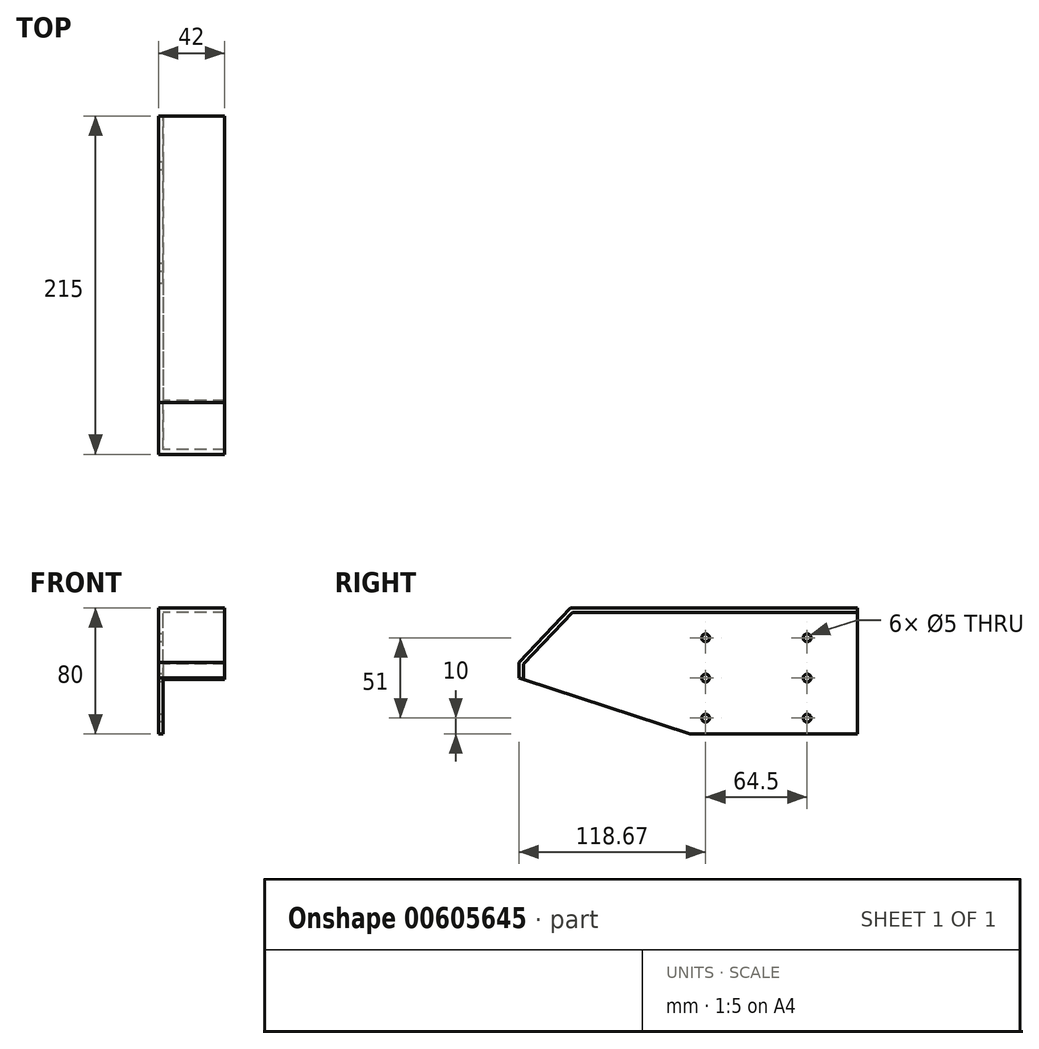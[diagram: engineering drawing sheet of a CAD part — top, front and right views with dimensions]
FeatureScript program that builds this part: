
annotation { "Feature Type Name" : "Feature", "Feature Type Description" : "" }
export const myFeature = defineFeature(function(context is Context, id is Id, definition is map)
    precondition{}
    {
        {
            var Q0;
            Q0=qCreatedBy(makeId("Right.planeOp"),FACE);
            var sketch = newSketch(context, id + "F0", { "sketchPlane" : qUnion([Q0])});
            skLineSegment(sketch, "E0.bottom", {"start": v(1.17, -40) * mm, "end": v(107.5, -40) * mm});
            skLineSegment(sketch, "E0.top", {"start": v(-74.63, 40) * mm, "end": v(107.5, 40) * mm});
            skLineSegment(sketch, "E0.right", {"start": v(107.5, -40) * mm, "end": v(107.5, 40) * mm});
            skPoint(sketch, "E0.middle", {"position": v(0, 0) * mm});
            skPoint(sketch, "E1", {"position": v(75.67, 40) * mm});
            skLineSegment(sketch, "E2", {"start": v(75.67, 40) * mm, "end": v(75.67, -40) * mm, "construction": true});
            skPoint(sketch, "E3", {"position": v(107.5, -30) * mm});
            skLineSegment(sketch, "E4", {"start": v(107.5, -30) * mm, "end": v(-107.5, -30) * mm, "construction": true});
            skCircle(sketch, "E5", {"center": v(75.67, -30) * mm, "radius": 2.5 * mm});
            skPoint(sketch, "E6", {"position": v(75.67, -4.5) * mm});
            skPoint(sketch, "E7", {"position": v(75.67, 21) * mm});
            skCircle(sketch, "E8", {"center": v(75.67, -4.5) * mm, "radius": 2.5 * mm});
            skCircle(sketch, "E9", {"center": v(75.67, 21) * mm, "radius": 2.5 * mm});
            skPoint(sketch, "E10", {"position": v(11.17, 21) * mm});
            skPoint(sketch, "E11", {"position": v(11.17, -4.5) * mm});
            skPoint(sketch, "E12", {"position": v(11.17, -30) * mm});
            skCircle(sketch, "E13", {"center": v(11.17, 21) * mm, "radius": 2.5 * mm});
            skCircle(sketch, "E14", {"center": v(11.17, -4.5) * mm, "radius": 2.5 * mm});
            skCircle(sketch, "E15", {"center": v(11.17, -30) * mm, "radius": 2.5 * mm});
            skLineSegment(sketch, "E16", {"start": v(11.17, -4.5) * mm, "end": v(-107.5, -4.5) * mm, "construction": true});
            skPoint(sketch, "E17", {"position": v(1.17, -30) * mm});
            skPoint(sketch, "E18", {"position": v(-65.23, -4.5) * mm});
            skPoint(sketch, "E19", {"position": v(-107.5, 5.5) * mm});
            skLineSegment(sketch, "E20", {"start": v(-107.5, 5.5) * mm, "end": v(-74.63, 40) * mm});
            skLineSegment(sketch, "E21", {"start": v(1.17, -40) * mm, "end": v(-107.5, -4.5) * mm});
            skPoint(sketch, "E22.orphan", {"position": v(-107.5, 40) * mm});
            skLineSegment(sketch, "E23.trimOffspring", {"start": v(-107.5, -4.5) * mm, "end": v(-107.5, 5.5) * mm});
            skPoint(sketch, "E24.orphan", {"position": v(-107.5, -40) * mm});
            skSolve(sketch);
        }
        {
            var Q0;
            Q0=makeQuery(id+"F0.imprint","IMPRINT",FACE,{"disambiguationData":[TD([[makeQuery(id+"F0.imprint","IMPRINT",EDGE,{"derivedFrom":sQuery(id+"F0.wireOp",EDGE,"E0.bottom")}),1.0]])]});
            extrude(context, id + "F1", {"entities" : qUnion([Q0]), "depth" : 3 * mm, "offsetDistance" : 25 * mm});
        }
        {
            var Q0;
            Q0=makeQuery(id+"F1.opExtrude","CAP_FACE",FACE,{"disambiguationData":[OSD([sQuery(id+"F0.wireOp",EDGE,"E0.bottom"),sQuery(id+"F0.wireOp",EDGE,"E0.top"),sQuery(id+"F0.wireOp",EDGE,"E0.right"),sQuery(id+"F0.wireOp",EDGE,"E5"),sQuery(id+"F0.wireOp",EDGE,"E8"),sQuery(id+"F0.wireOp",EDGE,"E9"),sQuery(id+"F0.wireOp",EDGE,"E13"),sQuery(id+"F0.wireOp",EDGE,"E14"),sQuery(id+"F0.wireOp",EDGE,"E15"),sQuery(id+"F0.wireOp",EDGE,"E20"),sQuery(id+"F0.wireOp",EDGE,"E21"),sQuery(id+"F0.wireOp",EDGE,"E23.trimOffspring")])],"isStart":false});
            var sketch = newSketch(context, id + "F2", { "sketchPlane" : qUnion([Q0])});
            skPoint(sketch, "E25", {"position": v(107.5, 37) * mm});
            skLineSegment(sketch, "E26", {"start": v(107.5, 37) * mm, "end": v(-73.34, 37) * mm});
            skLineSegment(sketch, "E27.0", {"start": v(-104.5, 4.3) * mm, "end": v(-73.34, 37) * mm});
            skPoint(sketch, "E28.endSnap0", {"position": v(-107.5, 0.5) * mm});
            skLineSegment(sketch, "E29.0", {"start": v(-104.5, -4.5) * mm, "end": v(-104.5, 4.3) * mm});
            skLineSegment(sketch, "E30", {"start": v(-104.5, -4.5) * mm, "end": v(-104.5, -5.48) * mm});
            skPoint(sketch, "E28.end.orphan", {"position": v(-107.5, 1.15) * mm});
            skSolve(sketch);
        }
        {
            var Q0;
            {var subQ2=sQuery(id+"F2.wireOp",EDGE,"E26");Q0=makeQuery(id+"F2.imprint","IMPRINT",FACE,{"disambiguationData":[TD([[makeQuery(id+"F2.imprint","IMPRINT",EDGE,{"derivedFrom":subQ2}),-1.0]])]});}
            extrude(context, id + "F3", {"entities" : qUnion([Q0]), "operationType" : NewBodyOperationType.ADD, "depth" : 39 * mm, "offsetDistance" : 25 * mm});
        }
    });
